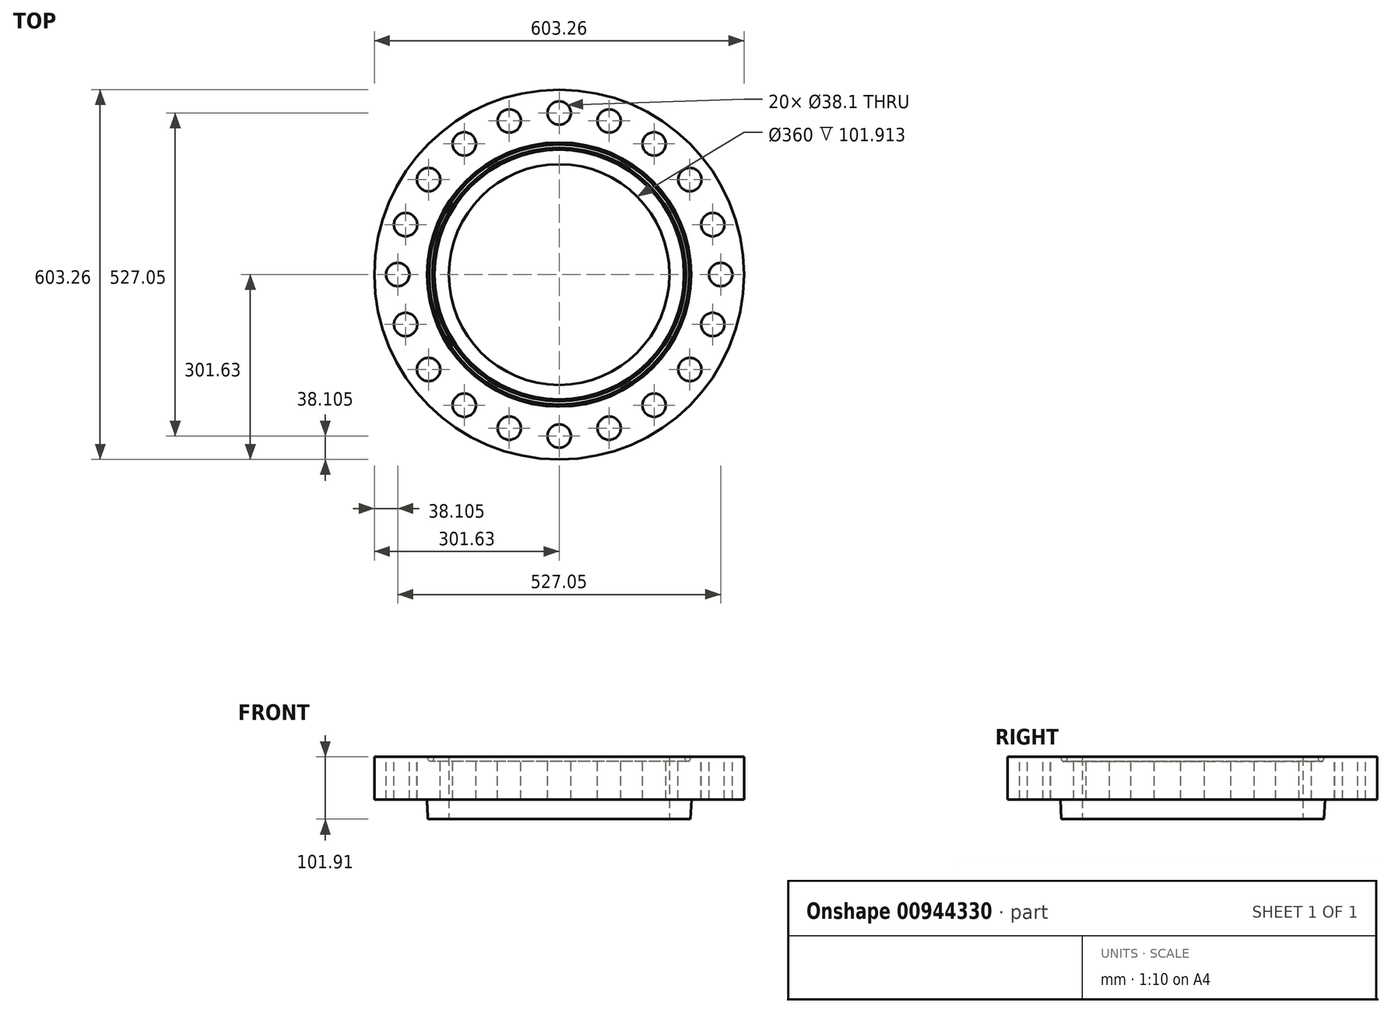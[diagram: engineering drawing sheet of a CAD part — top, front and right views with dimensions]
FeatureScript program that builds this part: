
annotation { "Feature Type Name" : "Feature", "Feature Type Description" : "" }
export const myFeature = defineFeature(function(context is Context, id is Id, definition is map)
    precondition{}
    {
        {
            var Q0;
            Q0=qCreatedBy(makeId("Top.planeOp"),FACE);
            var sketch = newSketch(context, id + "F0", { "sketchPlane" : qUnion([Q0])});
            skCircle(sketch, "E0", {"center": v(0, 0) * mm, "radius": 301.63 * mm});
            skSolve(sketch);
        }
        {
            var Q0;
            Q0=makeQuery(id+"F0.imprint","IMPRINT",FACE,{"disambiguationData":[TD([[makeQuery(id+"F0.imprint","IMPRINT",EDGE,{"derivedFrom":sQuery(id+"F0.wireOp",EDGE,"E0")}),1.0]])]});
            extrude(context, id + "F1", {"entities" : qUnion([Q0]), "oppositeDirection" : true, "depth" : 69.85 * mm, "offsetDistance" : 25 * mm});
        }
        {
            var Q0;
            Q0=makeQuery(id+"F1.opExtrude","CAP_FACE",FACE,{"disambiguationData":[OSD([sQuery(id+"F0.wireOp",EDGE,"E0")])],"isStart":false});
            var sketch = newSketch(context, id + "F2", { "sketchPlane" : qUnion([Q0])});
            skCircle(sketch, "E1", {"center": v(0, 0) * mm, "radius": 215.9 * mm});
            skSolve(sketch);
        }
        {
            var Q0;
            Q0 = qSketchRegion(id + "F2", true);
            extrude(context, id + "F3", {"entities" : qUnion([Q0]), "operationType" : NewBodyOperationType.ADD, "depth" : 32.06 * mm, "offsetDistance" : 25 * mm, "hasDraft" : true, "draftAngle" : 3 * degree, "draftPullDirection" : true});
        }
        {
            var Q0;
            Q0=makeQuery(id+"F3.opExtrude","CAP_FACE",FACE,{"disambiguationData":[OSD([sQuery(id+"F2.wireOp",EDGE,"E1")])],"isStart":false});
            var sketch = newSketch(context, id + "F4", { "sketchPlane" : qUnion([Q0])});
            skCircle(sketch, "E2", {"center": v(0, 0) * mm, "radius": 180 * mm});
            skSolve(sketch);
        }
        {
            var Q0;
            Q0 = qSketchRegion(id + "F4", true);
            extrude(context, id + "F5", {"entities" : qUnion([Q0]), "operationType" : NewBodyOperationType.REMOVE, "endBound" : BoundingType.THROUGH_ALL, "oppositeDirection" : true, "depth" : 25 * mm, "offsetDistance" : 25 * mm});
        }
        {
            var Q0;
            Q0=qCreatedBy(makeId("Front.planeOp"),FACE);
            var sketch = newSketch(context, id + "F6", { "sketchPlane" : qUnion([Q0])});
            skLineSegment(sketch, "E3", {"start": v(209.55, 0) * mm, "end": v(215.5, 0) * mm});
            skLineSegment(sketch, "E4", {"start": v(203.6, 0) * mm, "end": v(209.55, 0) * mm});
            skLineSegment(sketch, "E5", {"start": v(209.55, 0) * mm, "end": v(209.55, -7.94) * mm});
            skLineSegment(sketch, "E6", {"start": v(203.6, 0) * mm, "end": v(206.97, -7.94) * mm});
            skLineSegment(sketch, "E7.MirrorCS", {"start": v(215.5, 0) * mm, "end": v(212.13, -7.94) * mm});
            skLineSegment(sketch, "E8", {"start": v(206.97, -7.94) * mm, "end": v(212.13, -7.94) * mm});
            skSolve(sketch);
        }
        {
            var Q0;
            Q0=makeQuery(id+"F1.opExtrude","CAP_FACE",FACE,{"disambiguationData":[OSD([sQuery(id+"F0.wireOp",EDGE,"E0")])],"isStart":true});
            var sketch = newSketch(context, id + "F7", { "sketchPlane" : qUnion([Q0])});
            skCircle(sketch, "E9", {"center": v(0, 0) * mm, "radius": 209.55 * mm});
            skSolve(sketch);
        }
        {
            var Q0;
            Q0 = qSketchRegion(id + "F6", true);
            var Q1;
            Q1=sQuery(id+"F7.wireOp",EDGE,"E9");
            revolve(context, id + "F8", {"operationType" : NewBodyOperationType.REMOVE, "surfaceOperationType" : NewSurfaceOperationType.NEW, "entities" : qUnion([Q0]), "axis" : qUnion([Q1]), "revolveType" : RevolveType.FULL, "oppositeDirection" : true});
        }
        {
            var Q0;
            {var subQ0=sQuery(id+"F0.wireOp",EDGE,"E0");Q0=makeQuery(id+"F8.boolean.opBoolean","SPLIT",FACE,{"disambiguationData":[TD([makeQuery(id+"F1.opExtrude","SWEPT_FACE",FACE,{"disambiguationData":[OSD([subQ0])]})])],"derivedFrom":makeQuery(id+"F1.opExtrude","CAP_FACE",FACE,{"disambiguationData":[OSD([subQ0])],"isStart":true})});}
            var sketch = newSketch(context, id + "F9", { "sketchPlane" : qUnion([Q0])});
            skPoint(sketch, "E10", {"position": v(263.53, 0) * mm});
            skPoint(sketch, "E11.1.0", {"position": v(250.63, 81.43) * mm});
            skPoint(sketch, "E11.2.0", {"position": v(213.2, 154.9) * mm});
            skPoint(sketch, "E11.center", {"position": v(0, 0) * mm});
            skPoint(sketch, "E12.0.3.0", {"position": v(154.9, 213.2) * mm});
            skPoint(sketch, "E12.0.4.0", {"position": v(81.43, 250.63) * mm});
            skPoint(sketch, "E12.0.5.0", {"position": v(0, 263.53) * mm});
            skPoint(sketch, "E12.0.6.0", {"position": v(-81.43, 250.63) * mm});
            skPoint(sketch, "E12.0.7.0", {"position": v(-154.9, 213.2) * mm});
            skPoint(sketch, "E12.0.8.0", {"position": v(-213.2, 154.9) * mm});
            skPoint(sketch, "E12.0.9.0", {"position": v(-250.63, 81.43) * mm});
            skPoint(sketch, "E12.0.10.0", {"position": v(-263.53, 0) * mm});
            skPoint(sketch, "E12.0.11.0", {"position": v(-250.63, -81.43) * mm});
            skPoint(sketch, "E12.0.12.0", {"position": v(-213.2, -154.9) * mm});
            skPoint(sketch, "E12.0.13.0", {"position": v(-154.9, -213.2) * mm});
            skPoint(sketch, "E12.0.14.0", {"position": v(-81.43, -250.63) * mm});
            skPoint(sketch, "E12.0.15.0", {"position": v(0, -263.53) * mm});
            skPoint(sketch, "E12.0.16.0", {"position": v(81.43, -250.63) * mm});
            skPoint(sketch, "E12.0.17.0", {"position": v(154.9, -213.2) * mm});
            skPoint(sketch, "E12.0.18.0", {"position": v(213.2, -154.9) * mm});
            skPoint(sketch, "E12.0.19.0", {"position": v(250.63, -81.43) * mm});
            skSolve(sketch);
        }
        {
            var Q0;
            Q0=sQuery(id+"F9.wireOp",VERTEX,"E10");
            var Q1;
            Q1=sQuery(id+"F9.wireOp",VERTEX,"E11.1.0");
            var Q2;
            Q2=sQuery(id+"F9.wireOp",VERTEX,"E11.2.0");
            var Q3;
            Q3=sQuery(id+"F9.wireOp",VERTEX,"E12.0.3.0");
            var Q4;
            Q4=sQuery(id+"F9.wireOp",VERTEX,"E12.0.4.0");
            var Q5;
            Q5=sQuery(id+"F9.wireOp",VERTEX,"E12.0.5.0");
            var Q6;
            Q6=sQuery(id+"F9.wireOp",VERTEX,"E12.0.6.0");
            var Q7;
            Q7=sQuery(id+"F9.wireOp",VERTEX,"E12.0.7.0");
            var Q8;
            Q8=sQuery(id+"F9.wireOp",VERTEX,"E12.0.8.0");
            var Q9;
            Q9=sQuery(id+"F9.wireOp",VERTEX,"E12.0.9.0");
            var Q10;
            Q10=sQuery(id+"F9.wireOp",VERTEX,"E12.0.10.0");
            var Q11;
            Q11=sQuery(id+"F9.wireOp",VERTEX,"E12.0.11.0");
            var Q12;
            Q12=sQuery(id+"F9.wireOp",VERTEX,"E12.0.12.0");
            var Q13;
            Q13=sQuery(id+"F9.wireOp",VERTEX,"E12.0.13.0");
            var Q14;
            Q14=sQuery(id+"F9.wireOp",VERTEX,"E12.0.14.0");
            var Q15;
            Q15=sQuery(id+"F9.wireOp",VERTEX,"E12.0.15.0");
            var Q16;
            Q16=sQuery(id+"F9.wireOp",VERTEX,"E12.0.16.0");
            var Q17;
            Q17=sQuery(id+"F9.wireOp",VERTEX,"E12.0.17.0");
            var Q18;
            Q18=sQuery(id+"F9.wireOp",VERTEX,"E12.0.18.0");
            var Q19;
            Q19=sQuery(id+"F9.wireOp",VERTEX,"E12.0.19.0");
            var Q20;
            Q20=makeQuery(id+"F1.opExtrude","SWEPT_BODY",BODY,{"disambiguationData":[OSD([sQuery(id+"F0.wireOp",EDGE,"E0")])]});
            hole(context, id + "F10", {"style" : HoleStyle.SIMPLE, "endStyle" : HoleEndStyle.THROUGH, "holeDiameter" : 38.1 * mm, "majorDiameter" : 5 * mm, "isTappedThrough" : true, "tappedDepth" : 12 * mm, "tapClearance" : 3, "locations" : qUnion([Q0, Q1, Q2, Q3, Q4, Q5, Q6, Q7, Q8, Q9, Q10, Q11, Q12, Q13, Q14, Q15, Q16, Q17, Q18, Q19]), "scope" : qUnion([Q20])});
        }
    });
